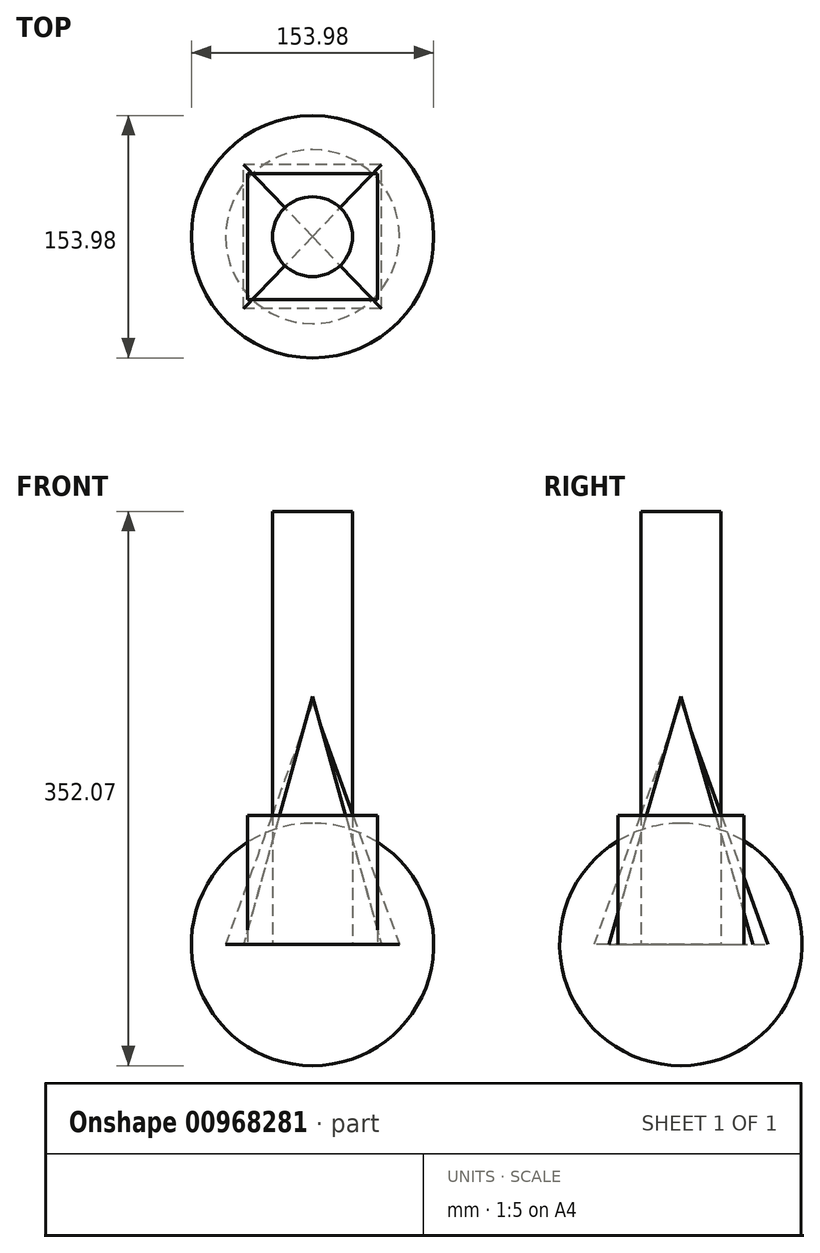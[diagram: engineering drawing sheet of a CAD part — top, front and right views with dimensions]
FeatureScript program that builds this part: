
annotation { "Feature Type Name" : "Feature", "Feature Type Description" : "" }
export const myFeature = defineFeature(function(context is Context, id is Id, definition is map)
    precondition{}
    {
        {
            var Q0;
            Q0=qCreatedBy(makeId("Front.planeOp"),FACE);
            var sketch = newSketch(context, id + "F0", { "sketchPlane" : qUnion([Q0])});
            skArc(sketch, "E0", {"start": v(0, 76.99) * mm, "mid": v(-76.99, 0) * mm, "end": v(0, -76.99) * mm});
            skLineSegment(sketch, "E1", {"start": v(0, -76.99) * mm, "end": v(0, 76.99) * mm});
            skSolve(sketch);
        }
        {
            var Q0;
            Q0=makeQuery(id+"F0.imprint","IMPRINT",FACE,{"disambiguationData":[TD([[makeQuery(id+"F0.imprint","IMPRINT",EDGE,{"derivedFrom":sQuery(id+"F0.wireOp",EDGE,"E0")}),1.0]])]});
            var Q1;
            Q1=sQuery(id+"F0.wireOp",EDGE,"E1");
            revolve(context, id + "F1", {"surfaceOperationType" : NewSurfaceOperationType.NEW, "entities" : qUnion([Q0]), "axis" : qUnion([Q1]), "revolveType" : RevolveType.FULL});
        }
        {
            var Q0;
            Q0=qCreatedBy(makeId("Top.planeOp"),FACE);
            var sketch = newSketch(context, id + "F2", { "sketchPlane" : qUnion([Q0])});
            skLineSegment(sketch, "E2.bottom", {"start": v(43.75, -45.83) * mm, "end": v(-43.75, -45.83) * mm});
            skLineSegment(sketch, "E2.top", {"start": v(43.75, 45.83) * mm, "end": v(-43.75, 45.83) * mm});
            skLineSegment(sketch, "E2.left", {"start": v(43.75, -45.83) * mm, "end": v(43.75, 45.83) * mm});
            skLineSegment(sketch, "E2.right", {"start": v(-43.75, -45.83) * mm, "end": v(-43.75, 45.83) * mm});
            skPoint(sketch, "E2.middle", {"position": v(0, 0) * mm});
            skSolve(sketch);
        }
        {
            var Q0;
            Q0=qCreatedBy(makeId("Front.planeOp"),FACE);
            var sketch = newSketch(context, id + "F3", { "sketchPlane" : qUnion([Q0])});
            skPoint(sketch, "E3", {"position": v(0, 157.65) * mm});
            skSolve(sketch);
        }
        {
            var Q0;
            Q0=sQuery(id+"F3.wireOp",VERTEX,"E3");
            var Q1;
            Q1 = qSketchRegion(id + "F2", true);
            loft(context, id + "F4", {"sheetProfilesArray" : [{ "sheetProfileEntities" : qUnion([Q0]) }, { "sheetProfileEntities" : qUnion([Q1]) }]});
        }
        {
            var Q0;
            Q0=qCreatedBy(makeId("Top.planeOp"),FACE);
            var sketch = newSketch(context, id + "F5", { "sketchPlane" : qUnion([Q0])});
            skLineSegment(sketch, "E4.bottom", {"start": v(41.19, -39.96) * mm, "end": v(-41.19, -39.96) * mm});
            skLineSegment(sketch, "E4.top", {"start": v(41.19, 39.96) * mm, "end": v(-41.19, 39.96) * mm});
            skLineSegment(sketch, "E4.left", {"start": v(41.19, -39.96) * mm, "end": v(41.19, 39.96) * mm});
            skLineSegment(sketch, "E4.right", {"start": v(-41.19, -39.96) * mm, "end": v(-41.19, 39.96) * mm});
            skPoint(sketch, "E4.middle", {"position": v(0, 0) * mm});
            skSolve(sketch);
        }
        {
            var Q0;
            Q0=makeQuery(id+"F5.imprint","IMPRINT",FACE,{"disambiguationData":[TD([[makeQuery(id+"F5.imprint","IMPRINT",EDGE,{"derivedFrom":sQuery(id+"F5.wireOp",EDGE,"E4.bottom")}),-1.0]])]});
            var Q1;
            Q1 = qSketchRegion(id + "F5", true);
            extrude(context, id + "F6", {"entities" : qUnion([Q0, Q1]), "depth" : 81.86 * mm, "offsetDistance" : 25.4 * mm});
        }
        {
            var Q0;
            Q0=qCreatedBy(makeId("Top.planeOp"),FACE);
            var sketch = newSketch(context, id + "F7", { "sketchPlane" : qUnion([Q0])});
            skCircle(sketch, "E5", {"center": v(0, 0) * mm, "radius": 55.22 * mm});
            skSolve(sketch);
        }
        {
            var Q0;
            Q0=qCreatedBy(makeId("Front.planeOp"),FACE);
            var sketch = newSketch(context, id + "F8", { "sketchPlane" : qUnion([Q0])});
            skPoint(sketch, "E6", {"position": v(0, 193.57) * mm});
            skPoint(sketch, "E7", {"position": v(0, 153.61) * mm});
            skSolve(sketch);
        }
        {
            var Q0;
            Q0 = qSketchRegion(id + "F7", true);
            var Q1;
            Q1=sQuery(id+"F8.wireOp",VERTEX,"E7");
            loft(context, id + "F9", {"sheetProfilesArray" : [{ "sheetProfileEntities" : qUnion([Q0]) }, { "sheetProfileEntities" : qUnion([Q1]) }]});
        }
        {
            var Q0;
            Q0=qCreatedBy(makeId("Top.planeOp"),FACE);
            var sketch = newSketch(context, id + "F10", { "sketchPlane" : qUnion([Q0])});
            skCircle(sketch, "E8", {"center": v(0, 0) * mm, "radius": 25.39 * mm});
            skSolve(sketch);
        }
        {
            var Q0;
            Q0=makeQuery(id+"F10.imprint","IMPRINT",FACE,{"disambiguationData":[TD([[makeQuery(id+"F10.imprint","IMPRINT",EDGE,{"derivedFrom":sQuery(id+"F10.wireOp",EDGE,"E8")}),1.0]])]});
            extrude(context, id + "F11", {"entities" : qUnion([Q0]), "depth" : 275.08 * mm, "offsetDistance" : 25.4 * mm});
        }
    });
